# Revit family: Hose-Stream-Rated_Smoke-Fire-Curtain_DoorSystems_DSI-HS10B-Over-Under
name_source: partatom
category: Doors
units: mm (PartAtom-declared; Revit-internal decimal feet)

## family parameters
Always vertical = Yes
Classification Number = 23.30.60.17
Cut with Voids When Loaded = No
Host = Wall
Room Calculation Point = No
Shared = No

## types (3) — shared parameters
Analytic Construction = <None>
CAD Details = https://www.arcat.com
CurtainDrop_Viz = Yes
Define Thermal Properties by = Schematic Type
Description = Hose Stream Rated Smoke and Fire Curtain
Fire Performance = UL 10B
Fire Rating = 1, 2, 3
Frame Width = 0' - 4"
FrameDepth = 0' - 2"
Keynote = 08 33 44
Manufacturer = Door Systems
Model = DSI-HS10B
Product Page URL = https://www.arcat.com
Rough Height = 0' - 0"
Rough Width = 0' - 0"
Specification = https://www.arcat.com
URL = https://www.doorsysinc.com
Wall Closure = By host

## per-type parameters (varying)
| type | HeadBox_Depth | HeadBox_Height |
| 9" x 15" Head-box #1 | 0' - 9" | 1' - 3" |
| 10" x 18" Head-box #2 | 0' - 10" | 1' - 6" |
| 12" x 21" Head-box #3 | 1' - 0" | 1' - 9" |

## geometry (parser evidence)
native form markers: Sweep x2
no freeform markers — native parametric forms only
